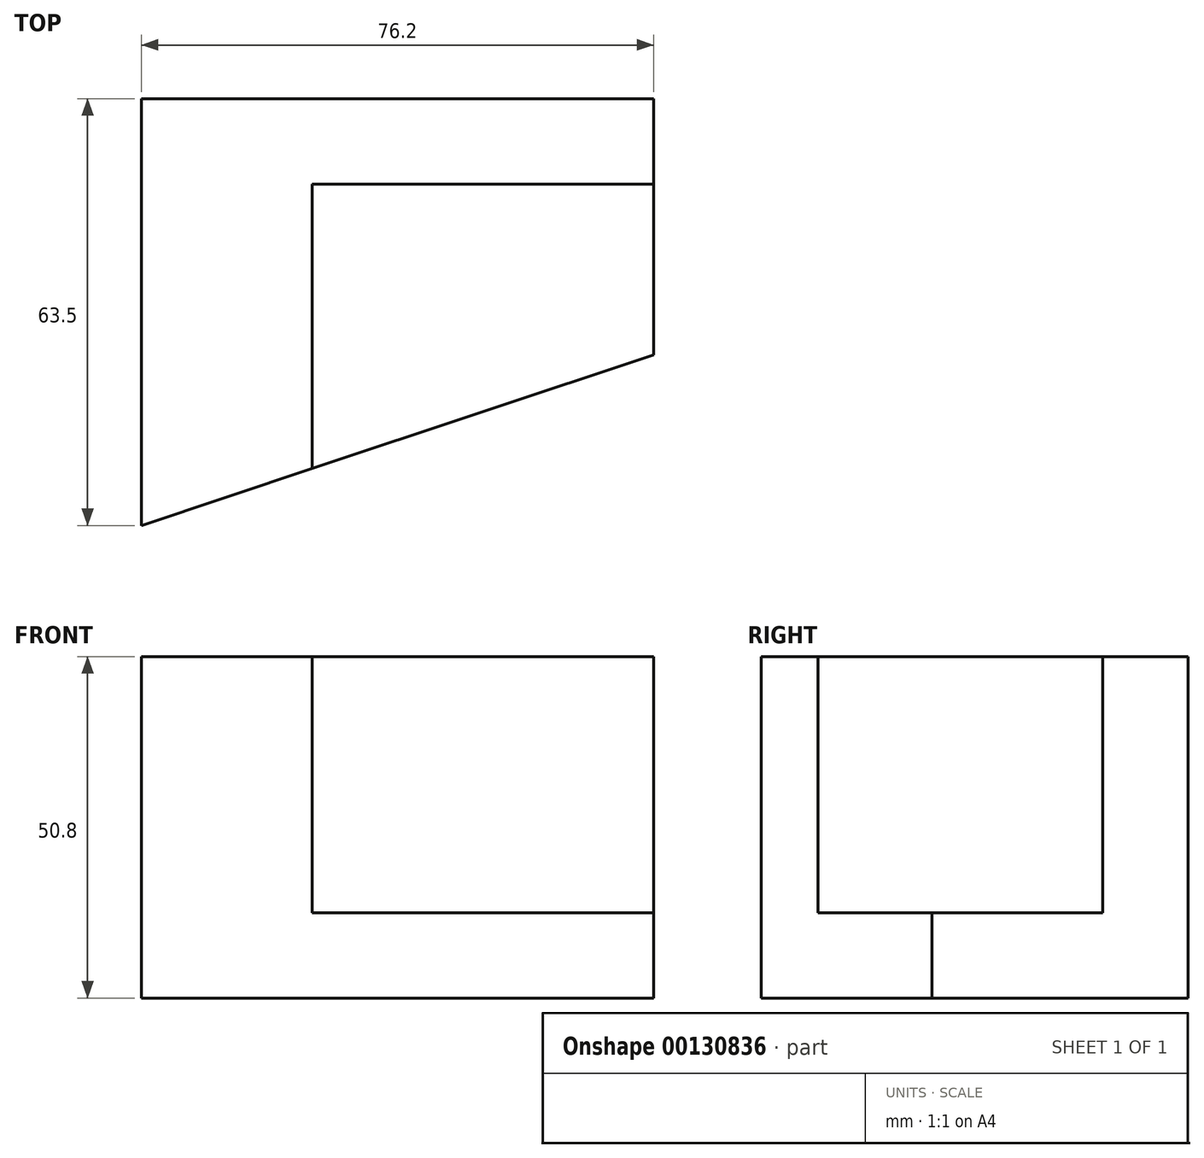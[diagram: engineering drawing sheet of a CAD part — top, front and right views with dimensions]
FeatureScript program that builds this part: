
annotation { "Feature Type Name" : "Feature", "Feature Type Description" : "" }
export const myFeature = defineFeature(function(context is Context, id is Id, definition is map)
    precondition{}
    {
        {
            var Q0;
            Q0=qCreatedBy(makeId("Front.planeOp"),FACE);
            var sketch = newSketch(context, id + "F0", { "sketchPlane" : qUnion([Q0])});
            skLineSegment(sketch, "E0", {"start": v(0, 0) * mm, "end": v(0, 50.8) * mm});
            skLineSegment(sketch, "E1", {"start": v(0, 50.8) * mm, "end": v(76.2, 50.8) * mm});
            skLineSegment(sketch, "E2", {"start": v(76.2, 50.8) * mm, "end": v(76.2, 0) * mm});
            skLineSegment(sketch, "E3", {"start": v(76.2, 0) * mm, "end": v(0, 0) * mm});
            skSolve(sketch);
        }
        {
            var Q0;
            Q0 = qSketchRegion(id + "F0", true);
            extrude(context, id + "F1", {"entities" : qUnion([Q0]), "oppositeDirection" : true, "depth" : 63.5 * mm});
        }
        {
            var Q0;
            Q0=makeQuery(id+"F1.opExtrude","SWEPT_FACE",FACE,{"disambiguationData":[OSD([sQuery(id+"F0.wireOp",EDGE,"E1")])]});
            var sketch = newSketch(context, id + "F2", { "sketchPlane" : qUnion([Q0])});
            skLineSegment(sketch, "E4", {"start": v(0, 0) * mm, "end": v(76.2, 25.4) * mm});
            skLineSegment(sketch, "E5", {"start": v(76.2, 25.4) * mm, "end": v(76.2, 0) * mm});
            skLineSegment(sketch, "E6", {"start": v(76.2, 0) * mm, "end": v(0, 0) * mm});
            skSolve(sketch);
        }
        {
            var Q0;
            Q0 = qSketchRegion(id + "F2", true);
            extrude(context, id + "F3", {"entities" : qUnion([Q0]), "operationType" : NewBodyOperationType.REMOVE, "endBound" : BoundingType.THROUGH_ALL, "oppositeDirection" : true, "depth" : 25.4 * mm});
        }
        {
            var Q0;
            Q0=makeQuery(id+"F1.opExtrude","SWEPT_FACE",FACE,{"disambiguationData":[OSD([sQuery(id+"F0.wireOp",EDGE,"E1")])]});
            var sketch = newSketch(context, id + "F4", { "sketchPlane" : qUnion([Q0])});
            skLineSegment(sketch, "E7", {"start": v(76.2, 50.8) * mm, "end": v(25.4, 50.8) * mm});
            skLineSegment(sketch, "E8", {"start": v(25.4, 50.8) * mm, "end": v(25.4, 8.47) * mm});
            skLineSegment(sketch, "E9", {"start": v(25.4, 8.47) * mm, "end": v(76.2, 25.4) * mm});
            skLineSegment(sketch, "E10", {"start": v(76.2, 25.4) * mm, "end": v(76.2, 50.8) * mm});
            skSolve(sketch);
        }
        {
            var Q0;
            Q0 = qSketchRegion(id + "F4", true);
            extrude(context, id + "F5", {"entities" : qUnion([Q0]), "operationType" : NewBodyOperationType.REMOVE, "oppositeDirection" : true, "depth" : 38.1 * mm});
        }
    });
